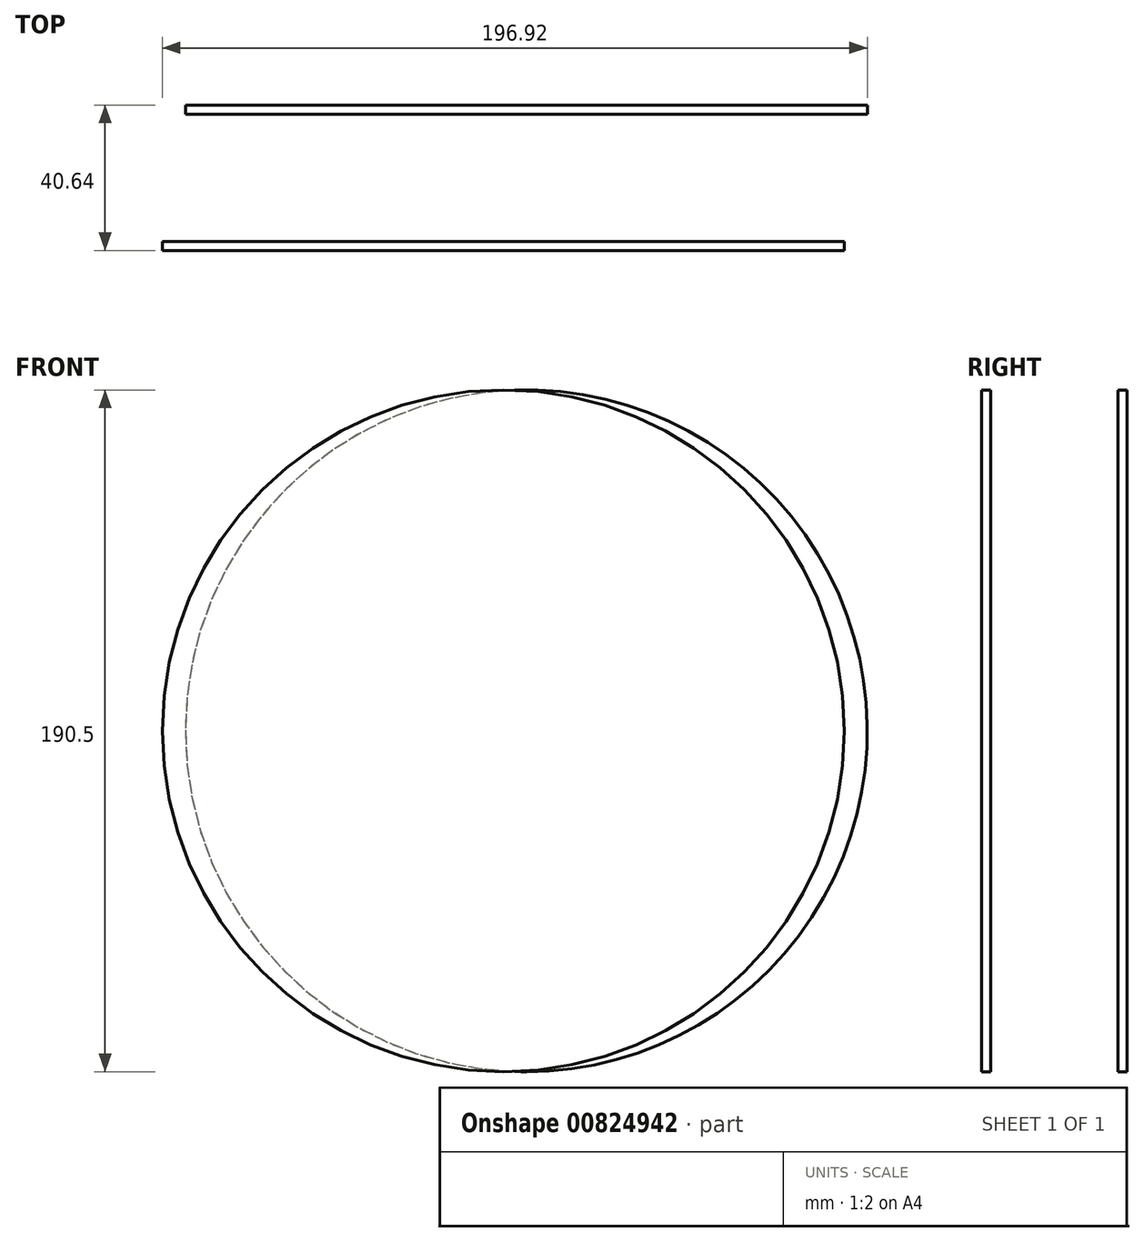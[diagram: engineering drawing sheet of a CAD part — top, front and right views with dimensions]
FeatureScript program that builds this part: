
annotation { "Feature Type Name" : "Feature", "Feature Type Description" : "" }
export const myFeature = defineFeature(function(context is Context, id is Id, definition is map)
    precondition{}
    {
        {
            var Q0;
            Q0=qCreatedBy(makeId("Front.planeOp"),FACE);
            var sketch = newSketch(context, id + "F0", { "sketchPlane" : qUnion([Q0])});
            skCircle(sketch, "E0", {"center": v(0, 0) * mm, "radius": 95.25 * mm});
            skSolve(sketch);
        }
        {
            var Q0;
            Q0=makeQuery(id+"F0.imprint","IMPRINT",FACE,{"disambiguationData":[TD([[makeQuery(id+"F0.imprint","IMPRINT",EDGE,{"derivedFrom":sQuery(id+"F0.wireOp",EDGE,"E0")}),1.0]])]});
            extrude(context, id + "F1", {"entities" : qUnion([Q0]), "depth" : 2.54 * mm, "offsetDistance" : 25.4 * mm});
        }
        {
            var Q0;
            Q0=qCreatedBy(makeId("Front.planeOp"),FACE);
            cPlane(context, id + "F2", {"entities" : qUnion([Q0]), "cplaneType" : CPlaneType.OFFSET, "offset" : 38.1 * mm, "width" : 152.4 * mm, "height" : 152.4 * mm});
        }
        {
            var Q0;
            Q0=qCreatedBy(id+"F2.planeOp",FACE);
            var sketch = newSketch(context, id + "F3", { "sketchPlane" : qUnion([Q0])});
            skCircle(sketch, "E1", {"center": v(-6.42, 0) * mm, "radius": 95.25 * mm});
            skSolve(sketch);
        }
        {
            var Q0;
            Q0 = qSketchRegion(id + "F3", true);
            extrude(context, id + "F4", {"entities" : qUnion([Q0]), "depth" : 2.54 * mm, "offsetDistance" : 25.4 * mm});
        }
    });
